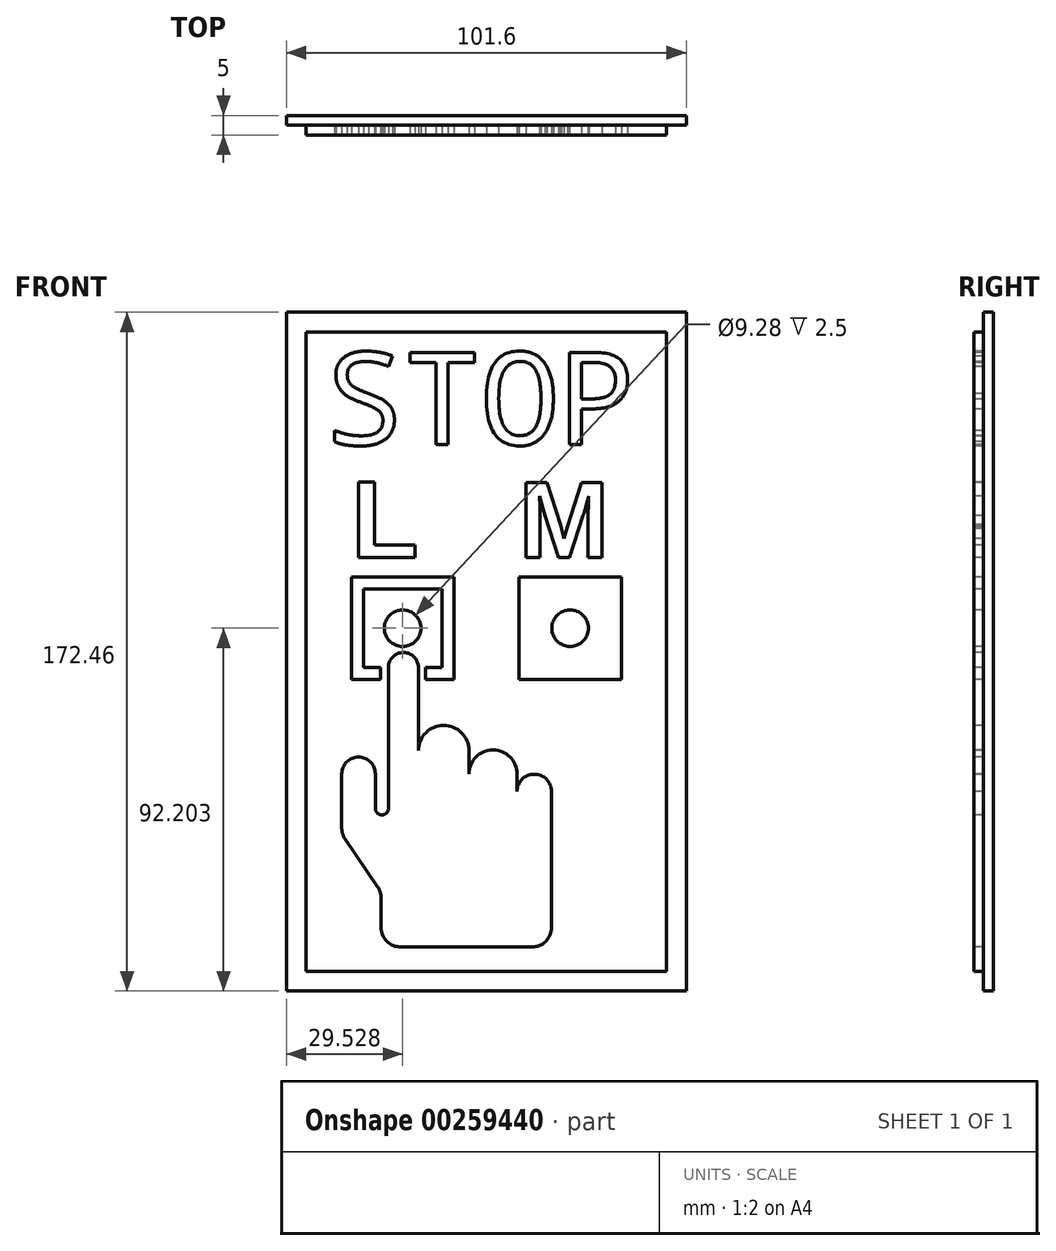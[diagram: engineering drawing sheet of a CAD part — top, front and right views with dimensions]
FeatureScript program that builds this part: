
annotation { "Feature Type Name" : "Feature", "Feature Type Description" : "" }
export const myFeature = defineFeature(function(context is Context, id is Id, definition is map)
    precondition{}
    {
        {
            var Q0;
            Q0=qCreatedBy(makeId("Front.planeOp"),FACE);
            var sketch = newSketch(context, id + "F0", { "sketchPlane" : qUnion([Q0])});
            skLineSegment(sketch, "E0.bottom", {"start": v(0, 0) * mm, "end": v(101.6, 0) * mm});
            skLineSegment(sketch, "E0.top", {"start": v(0, 203.2) * mm, "end": v(101.6, 203.2) * mm});
            skLineSegment(sketch, "E0.left", {"start": v(0, 0) * mm, "end": v(0, 203.2) * mm});
            skLineSegment(sketch, "E0.right", {"start": v(101.6, 0) * mm, "end": v(101.6, 203.2) * mm});
            skLineSegment(sketch, "E1.0", {"start": v(5, 5) * mm, "end": v(5, 198.2) * mm});
            skLineSegment(sketch, "E1.1", {"start": v(5, 5) * mm, "end": v(96.6, 5) * mm});
            skLineSegment(sketch, "E1.2", {"start": v(96.6, 5) * mm, "end": v(96.6, 198.2) * mm});
            skLineSegment(sketch, "E1.3", {"start": v(5, 198.2) * mm, "end": v(96.6, 198.2) * mm});
            skSolve(sketch);
        }
        {
            var Q0;
            Q0=makeQuery(id+"F0.imprint","IMPRINT",FACE,{"disambiguationData":[TD([[makeQuery(id+"F0.imprint","IMPRINT",EDGE,{"derivedFrom":sQuery(id+"F0.wireOp",EDGE,"E1.0")}),-1.0]])]});
            extrude(context, id + "F1", {"entities" : qUnion([Q0]), "depth" : 5 * mm, "offsetDistance" : 25 * mm});
        }
        {
            var Q0;
            Q0=makeQuery(id+"F0.imprint","IMPRINT",FACE,{"disambiguationData":[TD([[makeQuery(id+"F0.imprint","IMPRINT",EDGE,{"derivedFrom":sQuery(id+"F0.wireOp",EDGE,"E0.bottom")}),1.0]])]});
            extrude(context, id + "F2", {"entities" : qUnion([Q0]), "operationType" : NewBodyOperationType.ADD, "depth" : 2.5 * mm, "offsetDistance" : 25 * mm});
        }
        {
            var Q0;
            Q0=makeQuery(id+"F1.opExtrude","CAP_FACE",FACE,{"disambiguationData":[OSD([sQuery(id+"F0.wireOp",EDGE,"E1.0"),sQuery(id+"F0.wireOp",EDGE,"E1.1"),sQuery(id+"F0.wireOp",EDGE,"E1.2"),sQuery(id+"F0.wireOp",EDGE,"E1.3")])],"isStart":false});
            var sketch = newSketch(context, id + "F3", { "sketchPlane" : qUnion([Q0])});
            skLineSegment(sketch, "E2.0", {"start": v(10, 10) * mm, "end": v(10, 193.2) * mm, "construction": true});
            skLineSegment(sketch, "E2.1", {"start": v(10, 10) * mm, "end": v(91.6, 10) * mm, "construction": true});
            skLineSegment(sketch, "E2.2", {"start": v(91.6, 10) * mm, "end": v(91.6, 193.2) * mm, "construction": true});
            skLineSegment(sketch, "E2.3", {"start": v(10, 193.2) * mm, "end": v(91.6, 193.2) * mm, "construction": true});
            skText(sketch, "E3", { "text": "STOP", "fontName": "DroidSansMono.ttf"});
            skLineSegment(sketch, "E4.bottom", {"start": v(19.53, 132.94) * mm, "end": v(39.53, 132.94) * mm});
            skLineSegment(sketch, "E4.top", {"start": v(19.53, 112.94) * mm, "end": v(39.53, 112.94) * mm});
            skLineSegment(sketch, "E4.left", {"start": v(19.53, 132.94) * mm, "end": v(19.53, 112.94) * mm});
            skLineSegment(sketch, "E4.right", {"start": v(39.53, 132.94) * mm, "end": v(39.53, 112.94) * mm});
            skPoint(sketch, "E4.middle", {"position": v(29.53, 122.94) * mm});
            skLineSegment(sketch, "E5.0", {"start": v(16.53, 135.94) * mm, "end": v(42.53, 135.94) * mm});
            skLineSegment(sketch, "E5.1", {"start": v(16.53, 135.94) * mm, "end": v(16.53, 109.94) * mm});
            skLineSegment(sketch, "E5.2", {"start": v(16.53, 109.94) * mm, "end": v(42.53, 109.94) * mm});
            skLineSegment(sketch, "E5.3", {"start": v(42.53, 135.94) * mm, "end": v(42.53, 109.94) * mm});
            skCircle(sketch, "E6", {"center": v(29.53, 122.94) * mm, "radius": 4.64 * mm});
            skLineSegment(sketch, "E7", {"start": v(10, 116.25) * mm, "end": v(10, 95.36) * mm});
            skLineSegment(sketch, "E8", {"start": v(24.06, 54.43) * mm, "end": v(24.06, 46.92) * mm});
            skLineSegment(sketch, "E9", {"start": v(29.06, 41.92) * mm, "end": v(57.08, 41.92) * mm});
            skLineSegment(sketch, "E10", {"start": v(57.08, 41.92) * mm, "end": v(62.35, 41.92) * mm});
            skLineSegment(sketch, "E11", {"start": v(67.35, 46.92) * mm, "end": v(67.35, 81.44) * mm});
            skLineSegment(sketch, "E12", {"start": v(25.91, 112.94) * mm, "end": v(25.91, 77.18) * mm});
            skLineSegment(sketch, "E13", {"start": v(23.19, 57.25) * mm, "end": v(14.93, 69.34) * mm});
            skLineSegment(sketch, "E14", {"start": v(14.06, 72.16) * mm, "end": v(14.06, 85.93) * mm});
            skArc(sketch, "E15", {"start": v(22.59, 85.93) * mm, "mid": v(18.32, 90.2) * mm, "end": v(14.06, 85.93) * mm});
            skLineSegment(sketch, "E16", {"start": v(22.59, 85.93) * mm, "end": v(22.59, 77.18) * mm});
            skArc(sketch, "E17", {"start": v(22.59, 77.18) * mm, "mid": v(24.25, 75.52) * mm, "end": v(25.91, 77.18) * mm});
            skArc(sketch, "E18", {"start": v(33.53, 112.94) * mm, "mid": v(29.72, 116.75) * mm, "end": v(25.91, 112.94) * mm});
            skLineSegment(sketch, "E19", {"start": v(33.53, 112.94) * mm, "end": v(33.53, 91.84) * mm});
            skLineSegment(sketch, "E20", {"start": v(23.9, 112.94) * mm, "end": v(23.9, 109.94) * mm});
            skLineSegment(sketch, "E21", {"start": v(35.28, 112.94) * mm, "end": v(35.28, 109.94) * mm});
            skLineSegment(sketch, "E22", {"start": v(50.8, 169.55) * mm, "end": v(50.8, 115.43) * mm, "construction": true});
            skCircle(sketch, "E23.MirrorC", {"center": v(72.07, 122.94) * mm, "radius": 4.64 * mm});
            skLineSegment(sketch, "E24.MirrorCS", {"start": v(59.07, 135.94) * mm, "end": v(59.07, 109.94) * mm});
            skLineSegment(sketch, "E25.MirrorCS", {"start": v(85.07, 109.94) * mm, "end": v(59.07, 109.94) * mm});
            skLineSegment(sketch, "E26.MirrorCS", {"start": v(85.07, 135.94) * mm, "end": v(85.07, 109.94) * mm});
            skLineSegment(sketch, "E27.MirrorCS", {"start": v(85.07, 135.94) * mm, "end": v(59.07, 135.94) * mm});
            skLineSegment(sketch, "E28.MirrorCS", {"start": v(62.07, 132.94) * mm, "end": v(62.07, 112.94) * mm});
            skLineSegment(sketch, "E29.MirrorCS", {"start": v(82.07, 132.94) * mm, "end": v(82.07, 112.94) * mm});
            skLineSegment(sketch, "E30.MirrorCS", {"start": v(82.07, 112.94) * mm, "end": v(62.07, 112.94) * mm});
            skLineSegment(sketch, "E31.MirrorCS", {"start": v(82.07, 132.94) * mm, "end": v(62.07, 132.94) * mm});
            skLineSegment(sketch, "E32.0", {"start": v(16.53, 140.94) * mm, "end": v(42.53, 140.94) * mm, "construction": true});
            skLineSegment(sketch, "E33.MirrorCS", {"start": v(85.07, 140.94) * mm, "end": v(59.07, 140.94) * mm, "construction": true});
            skText(sketch, "E34", { "text": "L", "fontName": "Arimo-Bold.ttf"});
            skText(sketch, "E35", { "text": "M", "fontName": "Arimo-Bold.ttf"});
            skPoint(sketch, "E36.visualSharp", {"position": v(14.06, 70.62) * mm});
            skArc(sketch, "E36.filletArc", {"start": v(14.06, 72.16) * mm, "mid": v(14.28, 70.69) * mm, "end": v(14.93, 69.34) * mm});
            skPoint(sketch, "E37.visualSharp", {"position": v(24.06, 55.98) * mm});
            skArc(sketch, "E37.filletArc", {"start": v(24.06, 54.43) * mm, "mid": v(23.84, 55.9) * mm, "end": v(23.19, 57.25) * mm});
            skPoint(sketch, "E38.visualSharp", {"position": v(24.06, 41.92) * mm});
            skArc(sketch, "E38.filletArc", {"start": v(24.06, 46.92) * mm, "mid": v(25.52, 43.39) * mm, "end": v(29.06, 41.92) * mm});
            skPoint(sketch, "E39.visualSharp", {"position": v(67.35, 41.92) * mm});
            skArc(sketch, "E39.filletArc", {"start": v(62.35, 41.92) * mm, "mid": v(65.89, 43.39) * mm, "end": v(67.35, 46.92) * mm});
            skArc(sketch, "E40", {"start": v(46.37, 91.84) * mm, "mid": v(39.95, 98.25) * mm, "end": v(33.53, 91.84) * mm});
            skLineSegment(sketch, "E41", {"start": v(46.37, 91.84) * mm, "end": v(46.37, 85.93) * mm});
            skArc(sketch, "E42", {"start": v(58.56, 85.93) * mm, "mid": v(52.46, 92.03) * mm, "end": v(46.37, 85.93) * mm});
            skLineSegment(sketch, "E43", {"start": v(58.56, 85.93) * mm, "end": v(58.56, 81.44) * mm});
            skArc(sketch, "E44", {"start": v(67.35, 81.44) * mm, "mid": v(62.96, 85.83) * mm, "end": v(58.56, 81.44) * mm});
            const initialGuessF3  = {"E3": [0.01, 0.16955, 1, 0, 0.02365], "E34": [0.01653, 0.14094, 1, 0, 0.01996], "E35": [0.05907, 0.14094, 1, 0, 0.01986]};
            skSetInitialGuess(sketch, initialGuessF3);
            skSolve(sketch);
        }
        {
            var Q0;
            Q0=makeQuery(id+"F3.imprint","IMPRINT",FACE,{"disambiguationData":[TD([[makeQuery(id+"F3.imprint","IMPRINT",EDGE,{"derivedFrom":sQuery(id+"F3.wireOp",EDGE,"E3.sketch_text.stroke-0")}),-1.0]])]});
            var Q1;
            Q1=makeQuery(id+"F3.imprint","IMPRINT",FACE,{"disambiguationData":[TD([[makeQuery(id+"F3.imprint","IMPRINT",EDGE,{"derivedFrom":sQuery(id+"F3.wireOp",EDGE,"E3.sketch_text.stroke-20")}),-1.0]])]});
            var Q2;
            Q2=makeQuery(id+"F3.imprint","IMPRINT",FACE,{"disambiguationData":[TD([[makeQuery(id+"F3.imprint","IMPRINT",EDGE,{"derivedFrom":sQuery(id+"F3.wireOp",EDGE,"bff1b2f7-5b43-40db-ad50-737210fc3e16.sketch_text.stroke-0")}),-1.0]])]});
            var Q3;
            Q3=makeQuery(id+"F3.imprint","IMPRINT",FACE,{"disambiguationData":[TD([[makeQuery(id+"F3.imprint","IMPRINT",EDGE,{"derivedFrom":sQuery(id+"F3.wireOp",EDGE,"bff1b2f7-5b43-40db-ad50-737210fc3e16.sketch_text.stroke-35")}),-1.0]])]});
            var Q4;
            Q4=makeQuery(id+"F3.imprint","IMPRINT",FACE,{"disambiguationData":[TD([[makeQuery(id+"F3.imprint","IMPRINT",EDGE,{"derivedFrom":sQuery(id+"F3.wireOp",EDGE,"bff1b2f7-5b43-40db-ad50-737210fc3e16.sketch_text.stroke-60")}),-1.0]])]});
            var Q5;
            Q5=makeQuery(id+"F3.imprint","IMPRINT",FACE,{"disambiguationData":[TD([[makeQuery(id+"F3.imprint","IMPRINT",EDGE,{"derivedFrom":sQuery(id+"F3.wireOp",EDGE,"bff1b2f7-5b43-40db-ad50-737210fc3e16.sketch_text.stroke-72")}),-1.0]])]});
            var Q6;
            Q6=makeQuery(id+"F3.imprint","IMPRINT",FACE,{"disambiguationData":[TD([[makeQuery(id+"F3.imprint","IMPRINT",EDGE,{"derivedFrom":sQuery(id+"F3.wireOp",EDGE,"E3.sketch_text.stroke-28")}),-1.0]])]});
            var Q7;
            Q7=makeQuery(id+"F3.imprint","IMPRINT",FACE,{"disambiguationData":[TD([[makeQuery(id+"F3.imprint","IMPRINT",EDGE,{"derivedFrom":sQuery(id+"F3.wireOp",EDGE,"E3.sketch_text.stroke-40")}),-1.0]])]});
            var Q8;
            Q8=makeQuery(id+"F3.imprint","IMPRINT",FACE,{"disambiguationData":[TD([[makeQuery(id+"F3.imprint","IMPRINT",EDGE,{"derivedFrom":sQuery(id+"F3.wireOp",EDGE,"E8")}),1.0]])]});
            var Q9;
            Q9=makeQuery(id+"F3.imprint","IMPRINT",FACE,{"disambiguationData":[TD([[makeQuery(id+"F3.imprint","IMPRINT",EDGE,{"derivedFrom":sQuery(id+"F3.wireOp",EDGE,"bff1b2f7-5b43-40db-ad50-737210fc3e16.sketch_text.stroke-20")}),-1.0]])]});
            var Q10;
            Q10=makeQuery(id+"F3.imprint","IMPRINT",FACE,{"disambiguationData":[TD([[makeQuery(id+"F3.imprint","IMPRINT",EDGE,{"derivedFrom":sQuery(id+"F3.wireOp",EDGE,"bff1b2f7-5b43-40db-ad50-737210fc3e16.sketch_text.stroke-45")}),-1.0]])]});
            var Q11;
            Q11=makeQuery(id+"F3.imprint","IMPRINT",FACE,{"disambiguationData":[TD([[makeQuery(id+"F3.imprint","IMPRINT",EDGE,{"derivedFrom":sQuery(id+"F3.wireOp",EDGE,"E4.bottom")}),1.0]])]});
            var Q12;
            {var subQ1=sQuery(id+"F3.wireOp",EDGE,"E12");var subQ6=sQuery(id+"F3.wireOp",EDGE,"E5.2");var subQ7=makeQuery(id+"F3.imprint","INTERSECT",VERTEX,{"derivedFrom":[subQ6,subQ1]});Q12=makeQuery(id+"F3.imprint","IMPRINT",FACE,{"disambiguationData":[TD([[makeQuery(id+"F3.imprint","IMPRINT",EDGE,{"disambiguationData":[TD([[subQ7,-1.0]])],"derivedFrom":subQ6}),1.0]])]});}
            var Q13;
            Q13=makeQuery(id+"F3.imprint","IMPRINT",FACE,{"disambiguationData":[TD([[makeQuery(id+"F3.imprint","IMPRINT",EDGE,{"derivedFrom":sQuery(id+"F3.wireOp",EDGE,"E6")}),1.0]])]});
            var Q14;
            {var subQ0=sQuery(id+"F3.wireOp",EDGE,"E18");Q14=makeQuery(id+"F3.imprint","IMPRINT",FACE,{"disambiguationData":[TD([[makeQuery(id+"F3.imprint","IMPRINT",EDGE,{"derivedFrom":subQ0}),1.0]])]});}
            var Q15;
            Q15=makeQuery(id+"F3.imprint","IMPRINT",FACE,{"disambiguationData":[TD([[makeQuery(id+"F3.imprint","IMPRINT",EDGE,{"derivedFrom":sQuery(id+"F3.wireOp",EDGE,"E24.MirrorCS")}),1.0]])]});
            var Q16;
            Q16=makeQuery(id+"F3.imprint","IMPRINT",FACE,{"disambiguationData":[TD([[makeQuery(id+"F3.imprint","IMPRINT",EDGE,{"derivedFrom":sQuery(id+"F3.wireOp",EDGE,"E23.MirrorC")}),-1.0]])]});
            var Q17;
            Q17=makeQuery(id+"F3.imprint","IMPRINT",FACE,{"disambiguationData":[TD([[makeQuery(id+"F3.imprint","IMPRINT",EDGE,{"derivedFrom":sQuery(id+"F3.wireOp",EDGE,"E34.sketch_text.stroke-0")}),-1.0]])]});
            var Q18;
            Q18=makeQuery(id+"F3.imprint","IMPRINT",FACE,{"disambiguationData":[TD([[makeQuery(id+"F3.imprint","IMPRINT",EDGE,{"derivedFrom":sQuery(id+"F3.wireOp",EDGE,"E35.sketch_text.stroke-0")}),-1.0]])]});
            extrude(context, id + "F4", {"entities" : qUnion([Q0, Q1, Q2, Q3, Q4, Q5, Q6, Q7, Q8, Q9, Q10, Q11, Q12, Q13, Q14, Q15, Q16, Q17, Q18]), "operationType" : NewBodyOperationType.REMOVE, "oppositeDirection" : true, "depth" : 2.5 * mm, "offsetDistance" : 25 * mm});
        }
        {
            var Q0;
            {var subQ7=sQuery(id+"F0.wireOp",EDGE,"E1.1");var subQ8=sQuery(id+"F0.wireOp",EDGE,"E1.0");var subQ10=sQuery(id+"F0.wireOp",EDGE,"E1.2");var subQ11=sQuery(id+"F0.wireOp",EDGE,"E1.3");Q0=makeQuery(id+"F4.boolean.opBoolean","SPLIT",FACE,{"disambiguationData":[TD([makeQuery(id+"F1.opExtrude","SWEPT_FACE",FACE,{"disambiguationData":[OSD([subQ8])]})])],"derivedFrom":makeQuery(id+"F1.opExtrude","CAP_FACE",FACE,{"disambiguationData":[OSD([subQ8,subQ7,subQ10,subQ11])],"isStart":false})});}
            var sketch = newSketch(context, id + "F5", { "sketchPlane" : qUnion([Q0])});
            skLineSegment(sketch, "E45", {"start": v(0, 35.74) * mm, "end": v(102.67, 35.74) * mm});
            skLineSegment(sketch, "E46", {"start": v(102.67, 35.74) * mm, "end": v(102.67, 0) * mm});
            skLineSegment(sketch, "E47", {"start": v(102.67, 0) * mm, "end": v(-3.36, 0) * mm});
            skLineSegment(sketch, "E48", {"start": v(-3.36, 0) * mm, "end": v(0, 35.74) * mm});
            skSolve(sketch);
        }
        {
            var Q0;
            Q0=qSketchRegion(id+"F5",true);
            extrude(context, id + "F6", {"entities" : qUnion([Q0]), "operationType" : NewBodyOperationType.REMOVE, "oppositeDirection" : true, "depth" : 2.5 * mm, "offsetDistance" : 25 * mm});
        }
        {
            var Q0;
            Q0=makeQuery(id+"F6.boolean.opBoolean","MERGE",FACE,{"derivedFrom":[makeQuery(id+"F2.opExtrude","CAP_FACE",FACE,{"disambiguationData":[OSD([sQuery(id+"F0.wireOp",EDGE,"E0.bottom"),sQuery(id+"F0.wireOp",EDGE,"E0.top"),sQuery(id+"F0.wireOp",EDGE,"E0.left"),sQuery(id+"F0.wireOp",EDGE,"E0.right"),sQuery(id+"F0.wireOp",EDGE,"E1.0"),sQuery(id+"F0.wireOp",EDGE,"E1.1"),sQuery(id+"F0.wireOp",EDGE,"E1.2"),sQuery(id+"F0.wireOp",EDGE,"E1.3")])],"isStart":false}),makeQuery(id+"F6.opExtrude","CAP_FACE",FACE,{"disambiguationData":[OSD([sQuery(id+"F5.wireOp",EDGE,"E45"),sQuery(id+"F5.wireOp",EDGE,"E46"),sQuery(id+"F5.wireOp",EDGE,"E47"),sQuery(id+"F5.wireOp",EDGE,"E48")])],"isStart":false})]});
            var sketch = newSketch(context, id + "F7", { "sketchPlane" : qUnion([Q0])});
            skLineSegment(sketch, "E49", {"start": v(5, 35.74) * mm, "end": v(5, 30.74) * mm});
            skLineSegment(sketch, "E50", {"start": v(5, 30.74) * mm, "end": v(0, 30.74) * mm});
            skLineSegment(sketch, "E51", {"start": v(0, 30.74) * mm, "end": v(0, 0) * mm});
            skLineSegment(sketch, "E52", {"start": v(0, 0) * mm, "end": v(101.6, 0) * mm});
            skLineSegment(sketch, "E53", {"start": v(101.6, 0) * mm, "end": v(101.6, 30.74) * mm});
            skLineSegment(sketch, "E54", {"start": v(101.6, 30.74) * mm, "end": v(5, 30.74) * mm});
            skSolve(sketch);
        }
        {
            var Q0;
            Q0=qSketchRegion(id+"F7",true);
            extrude(context, id + "F8", {"entities" : qUnion([Q0]), "operationType" : NewBodyOperationType.REMOVE, "endBound" : BoundingType.THROUGH_ALL, "oppositeDirection" : true, "depth" : 25 * mm, "offsetDistance" : 25 * mm});
        }
    });
